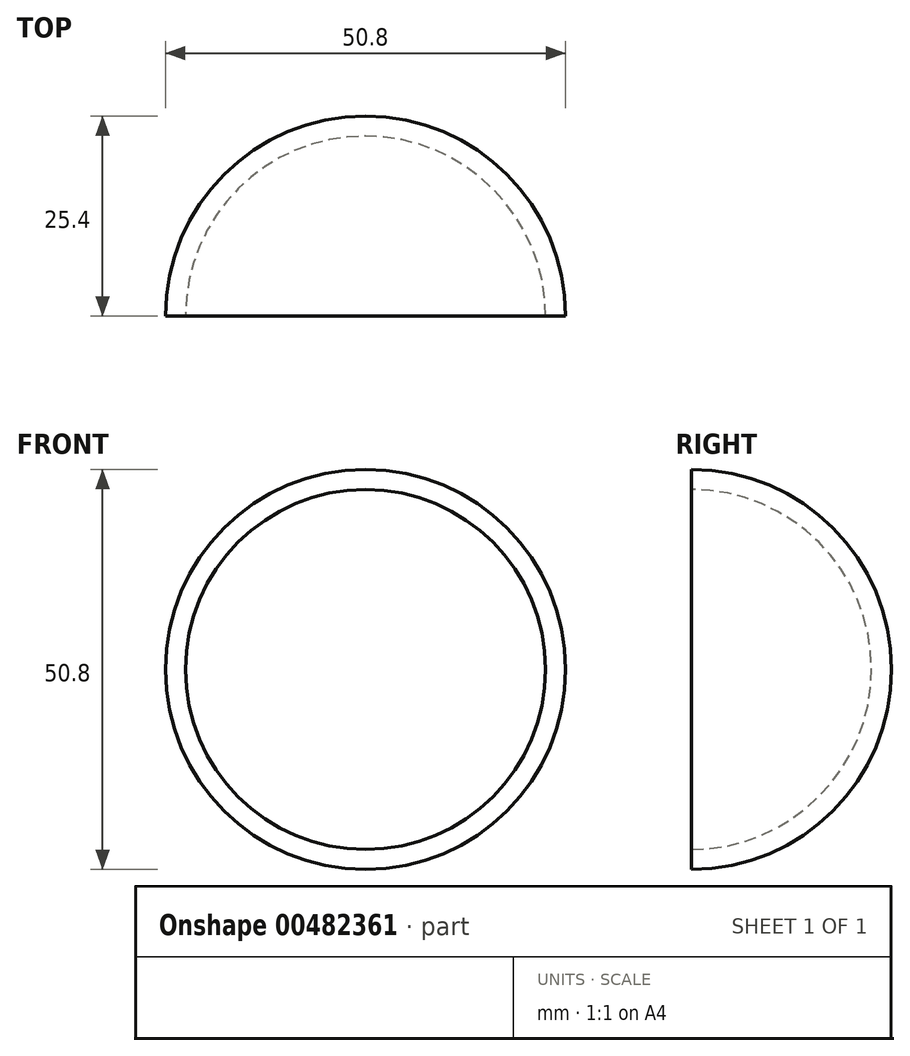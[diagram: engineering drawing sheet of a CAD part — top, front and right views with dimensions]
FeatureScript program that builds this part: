
annotation { "Feature Type Name" : "Feature", "Feature Type Description" : "" }
export const myFeature = defineFeature(function(context is Context, id is Id, definition is map)
    precondition{}
    {
        {
            var Q0;
            Q0=qCreatedBy(makeId("Front.planeOp"),FACE);
            var sketch = newSketch(context, id + "F0", { "sketchPlane" : qUnion([Q0])});
            skArc(sketch, "E0", {"start": v(0, -25.4) * mm, "mid": v(25.4, 0) * mm, "end": v(0, 25.4) * mm});
            skLineSegment(sketch, "E1", {"start": v(0, 0) * mm, "end": v(0, 70.1) * mm, "construction": true});
            skLineSegment(sketch, "E2", {"start": v(0, 25.4) * mm, "end": v(0, -25.4) * mm});
            skSolve(sketch);
        }
        {
            var Q0;
            Q0=makeQuery(id+"F0.imprint","IMPRINT",FACE,{"disambiguationData":[TD([[makeQuery(id+"F0.imprint","IMPRINT",EDGE,{"derivedFrom":sQuery(id+"F0.wireOp",EDGE,"E0")}),1.0]])]});
            var Q1;
            Q1=sQuery(id+"F0.wireOp",EDGE,"E1");
            revolve(context, id + "F1", {"entities" : qUnion([Q0]), "axis" : qUnion([Q1]), "revolveType" : RevolveType.ONE_DIRECTION, "angle" : 180 * degree});
        }
        {
            var Q0;
            Q0=makeQuery(id+"F1.opRevolve","CAP_FACE",FACE,{"disambiguationData":[OSD([sQuery(id+"F0.wireOp",EDGE,"E0"),sQuery(id+"F0.wireOp",EDGE,"E2")])],"isStart":true});
            shell(context, id + "F2", {"entities" : qUnion([Q0]), "thickness" : 2.54 * mm});
        }
    });
